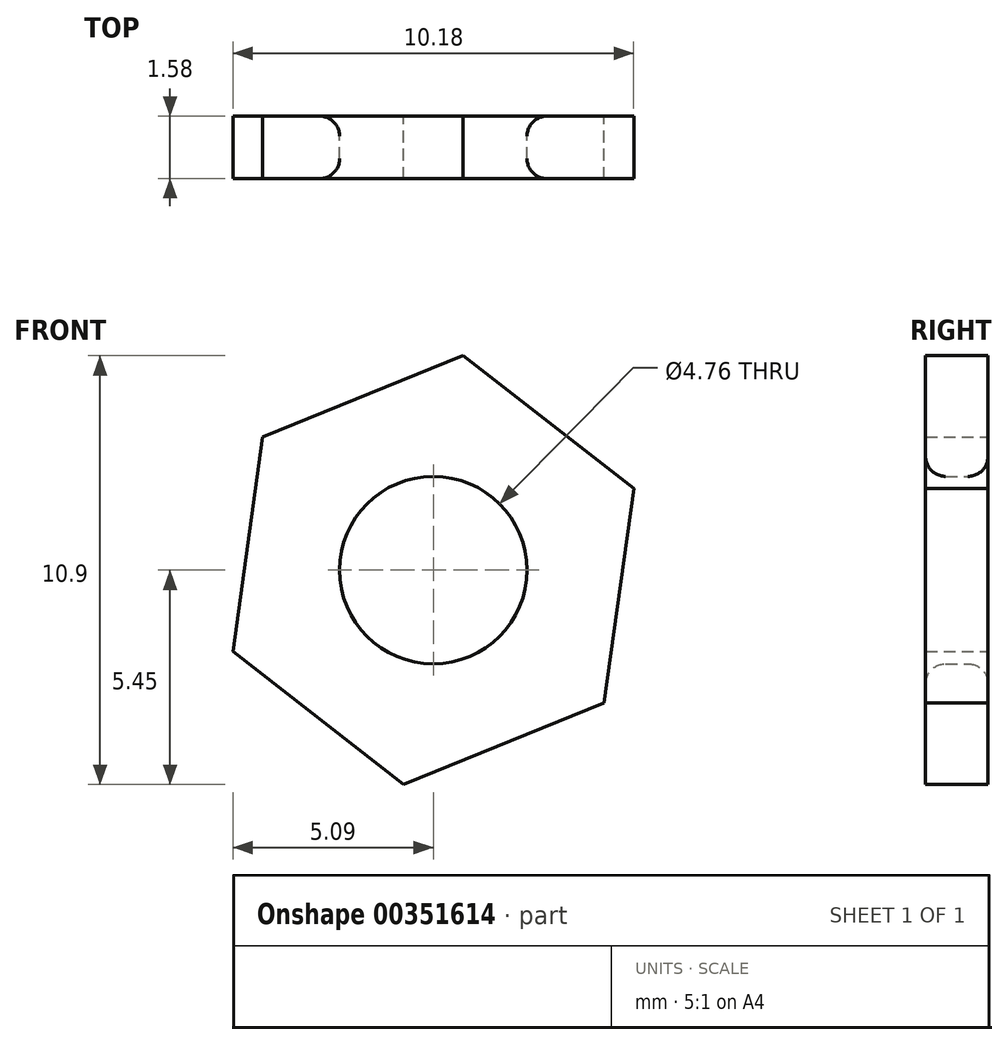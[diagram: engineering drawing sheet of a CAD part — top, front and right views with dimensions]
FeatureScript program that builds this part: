
annotation { "Feature Type Name" : "Feature", "Feature Type Description" : "" }
export const myFeature = defineFeature(function(context is Context, id is Id, definition is map)
    precondition{}
    {
        {
            var Q0;
            Q0=qCreatedBy(makeId("Front.planeOp"),FACE);
            var sketch = newSketch(context, id + "F0", { "sketchPlane" : qUnion([Q0])});
            skCircle(sketch, "E0", {"center": v(0, 0) * mm, "radius": 2.38 * mm});
            skCircle(sketch, "E1.cCircle", {"center": v(0, 0) * mm, "radius": 4.76 * mm, "construction": true});
            skLineSegment(sketch, "E1.0", {"start": v(-4.34, 3.38) * mm, "end": v(0.75, 5.45) * mm});
            skLineSegment(sketch, "E1.1", {"start": v(0.75, 5.45) * mm, "end": v(5.1, 2.07) * mm});
            skLineSegment(sketch, "E1.2", {"start": v(5.1, 2.07) * mm, "end": v(4.34, -3.38) * mm});
            skLineSegment(sketch, "E1.3", {"start": v(4.34, -3.38) * mm, "end": v(-0.75, -5.45) * mm});
            skLineSegment(sketch, "E1.4", {"start": v(-0.75, -5.45) * mm, "end": v(-5.1, -2.07) * mm});
            skLineSegment(sketch, "E1.5", {"start": v(-5.1, -2.07) * mm, "end": v(-4.34, 3.38) * mm});
            skPoint(sketch, "E1.0.midPoint", {"position": v(-1.8, 4.41) * mm});
            skSolve(sketch);
        }
        {
            var Q0;
            Q0 = qSketchRegion(id + "F0", true);
            extrude(context, id + "F1", {"entities" : qUnion([Q0]), "depth" : 1.59 * mm, "symmetric" : true});
        }
        {
            var Q0;
            Q0=makeQuery(id+"F1.opExtrude","CAP_EDGE",EDGE,{"disambiguationData":[OSD([sQuery(id+"F0.wireOp",EDGE,"E0")])],"isStart":false});
            fillet(context, id + "F2", {"entities" : qUnion([Q0]), "radius" : 0.5 * mm, "tangentPropagation" : true, "allowEdgeOverflow" : false});
        }
        {
            var Q0;
            Q0=makeQuery(id+"F1.opExtrude","CAP_EDGE",EDGE,{"disambiguationData":[OSD([sQuery(id+"F0.wireOp",EDGE,"E0")])],"isStart":true});
            fillet(context, id + "F3", {"entities" : qUnion([Q0]), "radius" : 0.5 * mm, "tangentPropagation" : true, "allowEdgeOverflow" : false});
        }
    });
